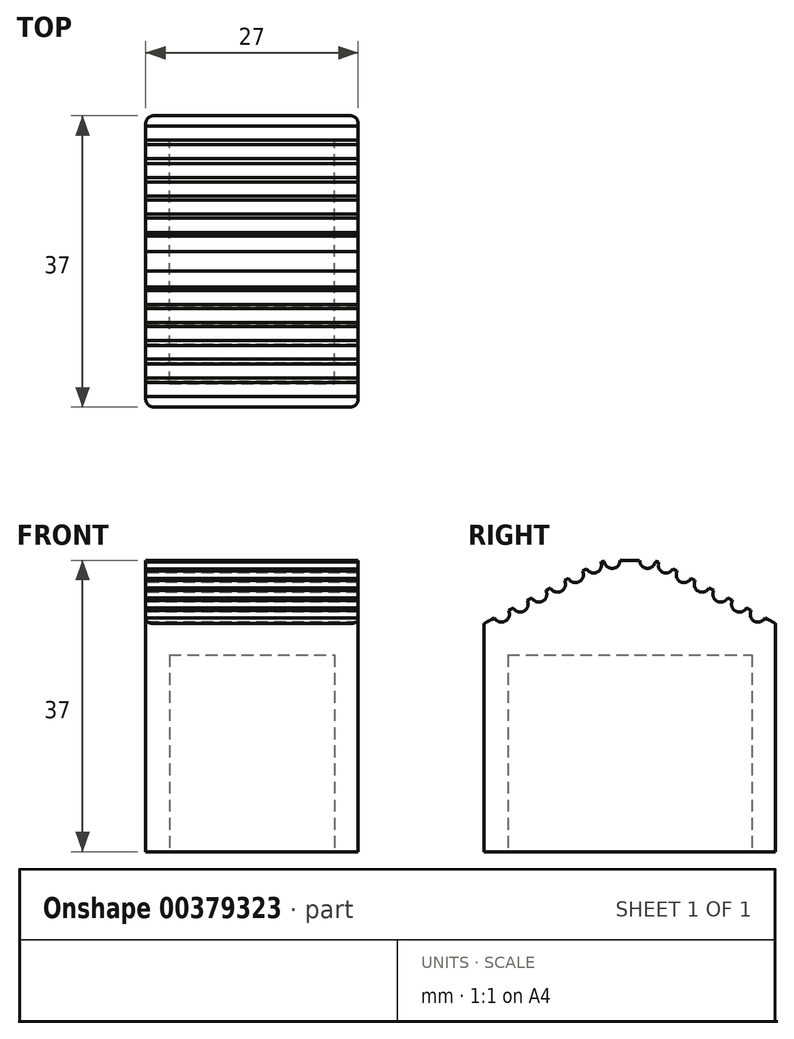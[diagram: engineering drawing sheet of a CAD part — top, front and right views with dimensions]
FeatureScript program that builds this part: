
annotation { "Feature Type Name" : "Feature", "Feature Type Description" : "" }
export const myFeature = defineFeature(function(context is Context, id is Id, definition is map)
    precondition{}
    {
        {
            var Q0;
            Q0=qCreatedBy(makeId("Top.planeOp"),FACE);
            var sketch = newSketch(context, id + "F0", { "sketchPlane" : qUnion([Q0])});
            skLineSegment(sketch, "E0.bottom", {"start": v(4.85, 5.56) * mm, "end": v(25.85, 5.56) * mm});
            skLineSegment(sketch, "E0.top", {"start": v(4.85, 36.56) * mm, "end": v(25.85, 36.56) * mm});
            skLineSegment(sketch, "E0.left", {"start": v(4.85, 5.56) * mm, "end": v(4.85, 36.56) * mm});
            skLineSegment(sketch, "E0.right", {"start": v(25.85, 5.56) * mm, "end": v(25.85, 36.56) * mm});
            skLineSegment(sketch, "E1.bottom", {"start": v(28.85, 39.56) * mm, "end": v(1.85, 39.56) * mm});
            skLineSegment(sketch, "E1.top", {"start": v(28.85, 2.56) * mm, "end": v(1.85, 2.56) * mm});
            skLineSegment(sketch, "E1.left", {"start": v(28.85, 39.56) * mm, "end": v(28.85, 2.56) * mm});
            skLineSegment(sketch, "E1.right", {"start": v(1.85, 39.56) * mm, "end": v(1.85, 2.56) * mm});
            skPoint(sketch, "E1.middle", {"position": v(15.35, 21.06) * mm});
            skPoint(sketch, "E1.middle.positionSnap0", {"position": v(25.85, 21.06) * mm});
            skPoint(sketch, "E1.middle.positionSnap1", {"position": v(15.35, 36.56) * mm});
            skPoint(sketch, "E1.centerSnap0", {"position": v(25.85, 21.06) * mm});
            skPoint(sketch, "E1.centerSnap1", {"position": v(15.35, 36.56) * mm});
            skSolve(sketch);
        }
        {
            var Q0;
            Q0 = qSketchRegion(id + "F0", true);
            extrude(context, id + "F1", {"entities" : qUnion([Q0]), "depth" : 25 * mm});
        }
        {
            var Q0;
            Q0=makeQuery(id+"F1.opExtrude","CAP_FACE",FACE,{"disambiguationData":[OSD([sQuery(id+"F0.wireOp",EDGE,"E0.bottom"),sQuery(id+"F0.wireOp",EDGE,"E0.top"),sQuery(id+"F0.wireOp",EDGE,"E0.left"),sQuery(id+"F0.wireOp",EDGE,"E0.right"),sQuery(id+"F0.wireOp",EDGE,"E1.bottom"),sQuery(id+"F0.wireOp",EDGE,"E1.top"),sQuery(id+"F0.wireOp",EDGE,"E1.left"),sQuery(id+"F0.wireOp",EDGE,"E1.right")])],"isStart":false});
            var sketch = newSketch(context, id + "F2", { "sketchPlane" : qUnion([Q0])});
            skLineSegment(sketch, "E2.bottom", {"start": v(1.85, 39.56) * mm, "end": v(28.85, 39.56) * mm});
            skLineSegment(sketch, "E2.top", {"start": v(1.85, 2.56) * mm, "end": v(28.85, 2.56) * mm});
            skLineSegment(sketch, "E2.left", {"start": v(1.85, 39.56) * mm, "end": v(1.85, 2.56) * mm});
            skLineSegment(sketch, "E2.right", {"start": v(28.85, 39.56) * mm, "end": v(28.85, 2.56) * mm});
            skSolve(sketch);
        }
        {
            var Q0;
            Q0 = qSketchRegion(id + "F2", true);
            extrude(context, id + "F3", {"entities" : qUnion([Q0]), "operationType" : NewBodyOperationType.ADD, "depth" : 12 * mm});
        }
        {
            var Q0;
            Q0=makeQuery(id+"F3.opExtrude","CAP_EDGE",EDGE,{"disambiguationData":[OSD([sQuery(id+"F2.wireOp",EDGE,"E2.bottom")])],"isStart":false});
            var Q1;
            Q1=makeQuery(id+"F3.opExtrude","CAP_EDGE",EDGE,{"disambiguationData":[OSD([sQuery(id+"F2.wireOp",EDGE,"E2.top")])],"isStart":false});
            chamfer(context, id + "F4", {"entities" : qUnion([Q0, Q1]), "chamferType" : ChamferType.TWO_OFFSETS, "width1" : 15 * mm, "oppositeDirection" : false, "width2" : 8 * mm, "tangentPropagation" : true});
        }
        {
            var Q0;
            {var subQ0=sQuery(id+"F2.wireOp",EDGE,"E2.bottom");Q0=makeQuery(id+"F4.opChamfer","BLEND_EDGE",EDGE,{"blendedFrom":[makeQuery(id+"F3.opExtrude","CAP_EDGE",EDGE,{"disambiguationData":[OSD([subQ0])],"isStart":false}),makeQuery(id+"F3.opExtrude","CAP_FACE",FACE,{"disambiguationData":[OSD([subQ0,sQuery(id+"F2.wireOp",EDGE,"E2.top"),sQuery(id+"F2.wireOp",EDGE,"E2.left"),sQuery(id+"F2.wireOp",EDGE,"E2.right")])],"isStart":false})],"blendedInto":[makeQuery(id+"F3.opExtrude","CAP_FACE",FACE,{"disambiguationData":[OSD([subQ0,sQuery(id+"F2.wireOp",EDGE,"E2.top"),sQuery(id+"F2.wireOp",EDGE,"E2.left"),sQuery(id+"F2.wireOp",EDGE,"E2.right")])],"isStart":false})]});}
            var Q1;
            {var subQ0=sQuery(id+"F2.wireOp",EDGE,"E2.top");Q1=makeQuery(id+"F4.opChamfer","BLEND_EDGE",EDGE,{"blendedFrom":[makeQuery(id+"F3.opExtrude","CAP_EDGE",EDGE,{"disambiguationData":[OSD([subQ0])],"isStart":false}),makeQuery(id+"F3.opExtrude","CAP_FACE",FACE,{"disambiguationData":[OSD([sQuery(id+"F2.wireOp",EDGE,"E2.bottom"),subQ0,sQuery(id+"F2.wireOp",EDGE,"E2.left"),sQuery(id+"F2.wireOp",EDGE,"E2.right")])],"isStart":false})],"blendedInto":[makeQuery(id+"F3.opExtrude","CAP_FACE",FACE,{"disambiguationData":[OSD([sQuery(id+"F2.wireOp",EDGE,"E2.bottom"),subQ0,sQuery(id+"F2.wireOp",EDGE,"E2.left"),sQuery(id+"F2.wireOp",EDGE,"E2.right")])],"isStart":false})]});}
            fillet(context, id + "F5", {"entities" : qUnion([Q0, Q1]), "radius" : 5 * mm, "tangentPropagation" : true, "allowEdgeOverflow" : false});
        }
        {
            var Q0;
            Q0=makeQuery(id+"F3.boolean.opBoolean","MERGE",FACE,{"derivedFrom":[makeQuery(id+"F1.opExtrude","SWEPT_FACE",FACE,{"disambiguationData":[OSD([sQuery(id+"F0.wireOp",EDGE,"E1.right")])]}),makeQuery(id+"F3.opExtrude","SWEPT_FACE",FACE,{"disambiguationData":[OSD([sQuery(id+"F2.wireOp",EDGE,"E2.left")])]})]});
            var sketch = newSketch(context, id + "F6", { "sketchPlane" : qUnion([Q0])});
            skCircle(sketch, "E3", {"center": v(-32.61, 32.7) * mm, "radius": 1 * mm});
            skCircle(sketch, "E4", {"center": v(-9.5, 32.7) * mm, "radius": 1 * mm});
            skCircle(sketch, "E5", {"center": v(-25.66, 36.41) * mm, "radius": 1 * mm});
            skCircle(sketch, "E6", {"center": v(-16.46, 36.41) * mm, "radius": 1 * mm});
            skCircle(sketch, "E7", {"center": v(-30.24, 33.97) * mm, "radius": 1 * mm});
            skCircle(sketch, "E8", {"center": v(-11.88, 33.97) * mm, "radius": 1 * mm});
            skCircle(sketch, "E9", {"center": v(-18.81, 37) * mm, "radius": 1 * mm});
            skCircle(sketch, "E10", {"center": v(-23.31, 37) * mm, "radius": 1 * mm});
            skCircle(sketch, "E11", {"center": v(-4.77, 30.18) * mm, "radius": 1 * mm});
            skCircle(sketch, "E12", {"center": v(-37.36, 30.18) * mm, "radius": 1 * mm});
            skCircle(sketch, "E13", {"center": v(-7.14, 31.44) * mm, "radius": 1 * mm});
            skCircle(sketch, "E14", {"center": v(-34.98, 31.44) * mm, "radius": 1 * mm});
            skCircle(sketch, "E15", {"center": v(-27.95, 35.2) * mm, "radius": 1 * mm});
            skCircle(sketch, "E16", {"center": v(-14.17, 35.2) * mm, "radius": 1 * mm});
            skSolve(sketch);
        }
        {
            var Q0;
            Q0 = qSketchRegion(id + "F6", true);
            extrude(context, id + "F7", {"entities" : qUnion([Q0]), "operationType" : NewBodyOperationType.REMOVE, "endBound" : BoundingType.THROUGH_ALL, "oppositeDirection" : true, "depth" : 25 * mm});
        }
        {
            var Q0;
            Q0=makeQuery(id+"F3.boolean.opBoolean","MERGE",EDGE,{"derivedFrom":[makeQuery(id+"F1.opExtrude","SWEPT_EDGE",EDGE,{"disambiguationData":[OSD([sQuery(id+"F0.wireOp",EDGE,"E1.bottom"),sQuery(id+"F0.wireOp",EDGE,"E1.left")])]}),makeQuery(id+"F3.opExtrude","SWEPT_EDGE",EDGE,{"disambiguationData":[OSD([sQuery(id+"F2.wireOp",EDGE,"E2.bottom"),sQuery(id+"F2.wireOp",EDGE,"E2.right")])]})]});
            var Q1;
            Q1=makeQuery(id+"F3.boolean.opBoolean","MERGE",EDGE,{"derivedFrom":[makeQuery(id+"F1.opExtrude","SWEPT_EDGE",EDGE,{"disambiguationData":[OSD([sQuery(id+"F0.wireOp",EDGE,"E1.bottom"),sQuery(id+"F0.wireOp",EDGE,"E1.right")])]}),makeQuery(id+"F3.opExtrude","SWEPT_EDGE",EDGE,{"disambiguationData":[OSD([sQuery(id+"F2.wireOp",EDGE,"E2.bottom"),sQuery(id+"F2.wireOp",EDGE,"E2.left")])]})]});
            var Q2;
            Q2=makeQuery(id+"F3.boolean.opBoolean","MERGE",EDGE,{"derivedFrom":[makeQuery(id+"F1.opExtrude","SWEPT_EDGE",EDGE,{"disambiguationData":[OSD([sQuery(id+"F0.wireOp",EDGE,"E1.top"),sQuery(id+"F0.wireOp",EDGE,"E1.left")])]}),makeQuery(id+"F3.opExtrude","SWEPT_EDGE",EDGE,{"disambiguationData":[OSD([sQuery(id+"F2.wireOp",EDGE,"E2.top"),sQuery(id+"F2.wireOp",EDGE,"E2.right")])]})]});
            var Q3;
            Q3=makeQuery(id+"F3.boolean.opBoolean","MERGE",EDGE,{"derivedFrom":[makeQuery(id+"F1.opExtrude","SWEPT_EDGE",EDGE,{"disambiguationData":[OSD([sQuery(id+"F0.wireOp",EDGE,"E1.top"),sQuery(id+"F0.wireOp",EDGE,"E1.right")])]}),makeQuery(id+"F3.opExtrude","SWEPT_EDGE",EDGE,{"disambiguationData":[OSD([sQuery(id+"F2.wireOp",EDGE,"E2.top"),sQuery(id+"F2.wireOp",EDGE,"E2.left")])]})]});
            fillet(context, id + "F8", {"entities" : qUnion([Q0, Q1, Q2, Q3]), "radius" : 1 * mm, "tangentPropagation" : true, "allowEdgeOverflow" : false});
        }
    });
